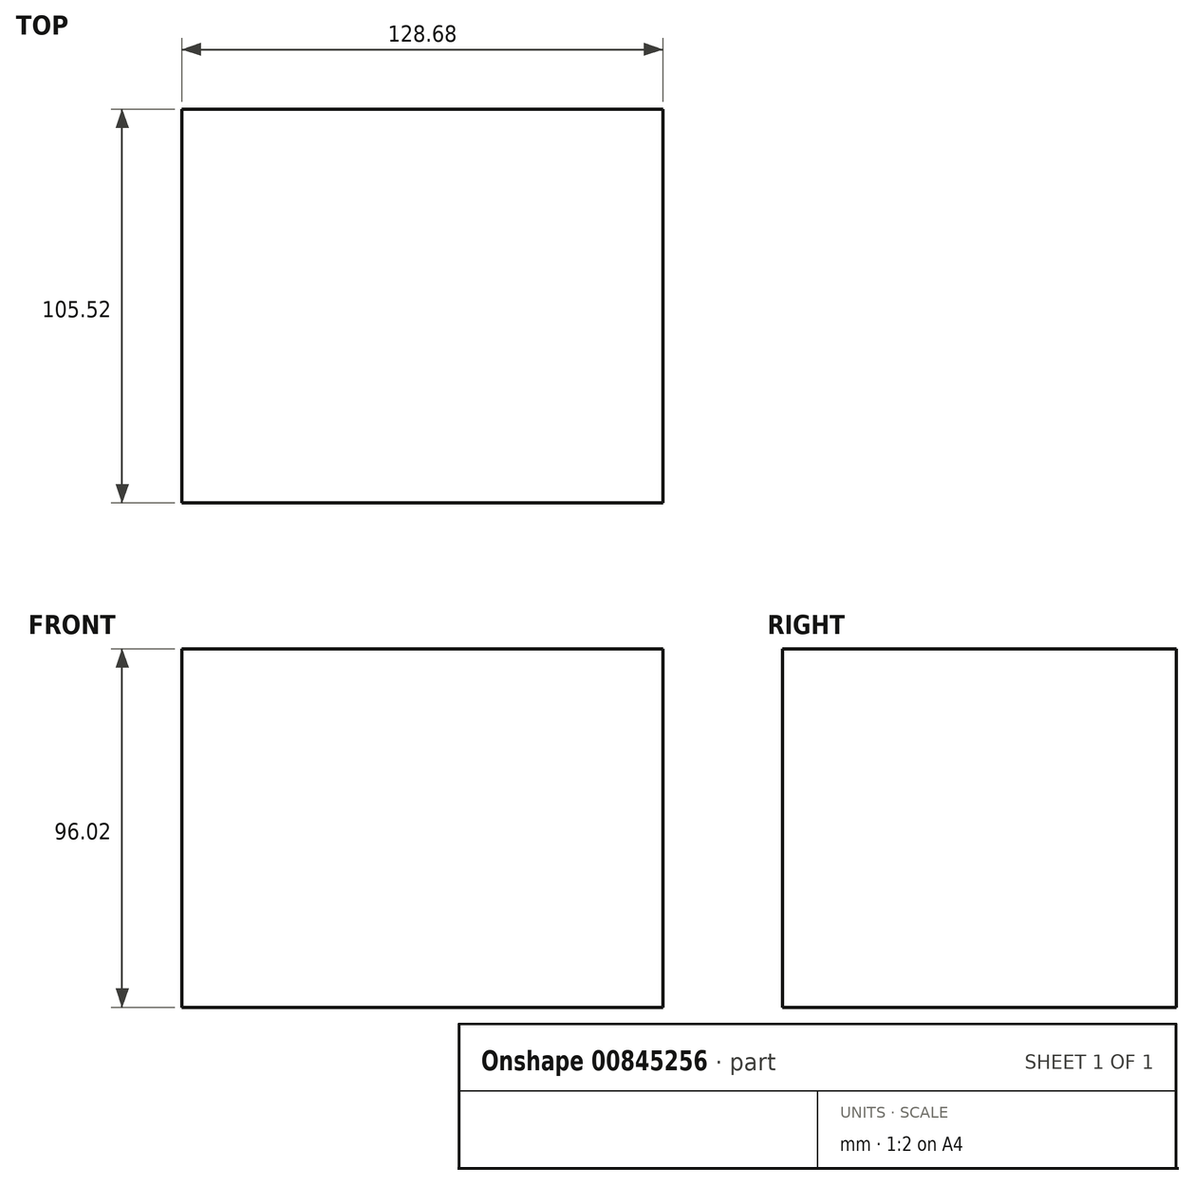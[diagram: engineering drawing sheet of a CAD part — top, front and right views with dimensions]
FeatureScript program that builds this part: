
annotation { "Feature Type Name" : "Feature", "Feature Type Description" : "" }
export const myFeature = defineFeature(function(context is Context, id is Id, definition is map)
    precondition{}
    {
        {
            var Q0;
            Q0=qCreatedBy(makeId("Top.planeOp"),FACE);
            var sketch = newSketch(context, id + "F0", { "sketchPlane" : qUnion([Q0])});
            skLineSegment(sketch, "E0.bottom", {"start": v(-64.34, -52.76) * mm, "end": v(64.34, -52.76) * mm});
            skLineSegment(sketch, "E0.top", {"start": v(-64.34, 52.76) * mm, "end": v(64.34, 52.76) * mm});
            skLineSegment(sketch, "E0.left", {"start": v(-64.34, -52.76) * mm, "end": v(-64.34, 52.76) * mm});
            skLineSegment(sketch, "E0.right", {"start": v(64.34, -52.76) * mm, "end": v(64.34, 52.76) * mm});
            skPoint(sketch, "E0.middle", {"position": v(0, 0) * mm});
            skSolve(sketch);
        }
        {
            var Q0;
            Q0=makeQuery(id+"F0.imprint","IMPRINT",FACE,{"disambiguationData":[TD([[makeQuery(id+"F0.imprint","IMPRINT",EDGE,{"derivedFrom":sQuery(id+"F0.wireOp",EDGE,"E0.bottom")}),1.0]])]});
            extrude(context, id + "F1", {"entities" : qUnion([Q0]), "endBound" : BoundingType.SYMMETRIC, "depth" : 96.01 * mm, "offsetDistance" : 25.4 * mm});
        }
    });
